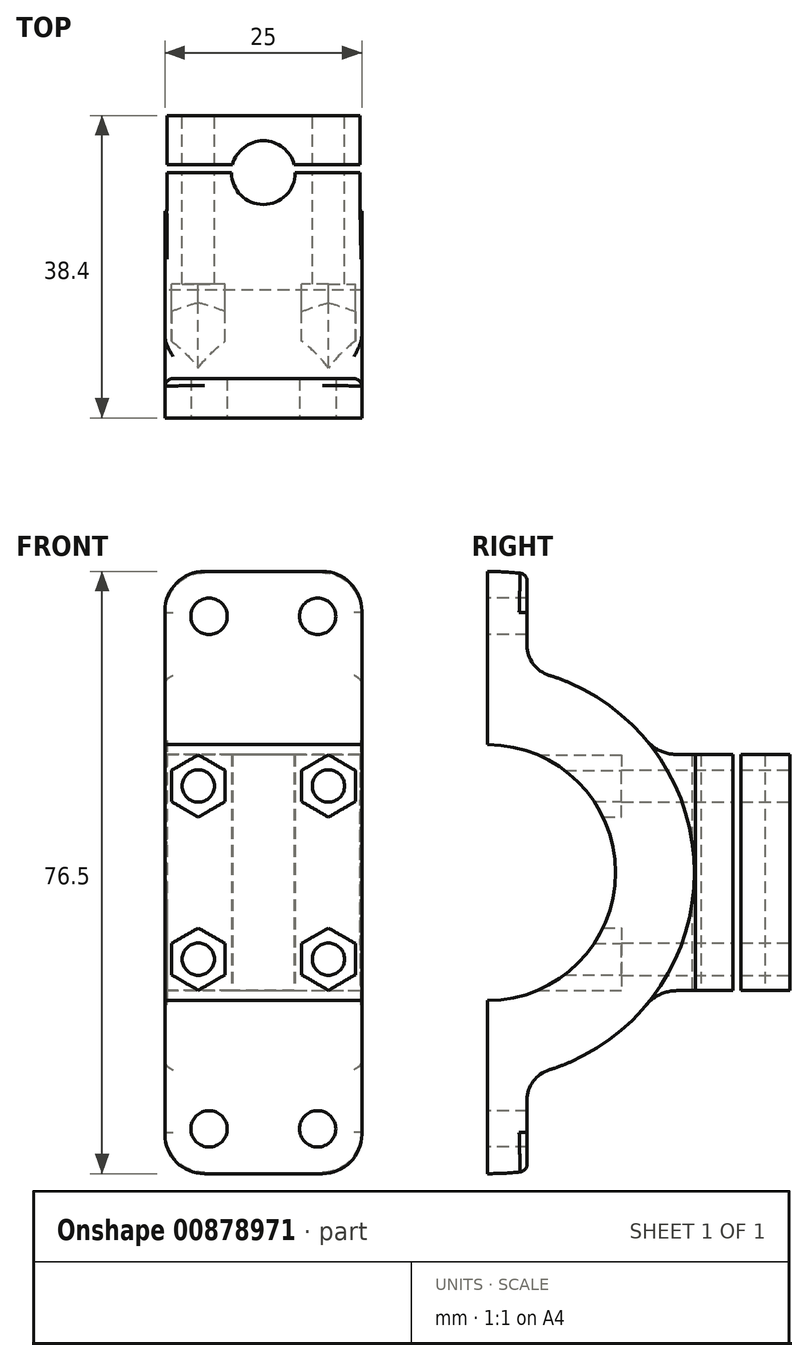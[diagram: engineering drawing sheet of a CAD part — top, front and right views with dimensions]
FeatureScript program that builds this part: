
annotation { "Feature Type Name" : "Feature", "Feature Type Description" : "" }
export const myFeature = defineFeature(function(context is Context, id is Id, definition is map)
    precondition{}
    {
        {
            var Q0;
            Q0=qCreatedBy(makeId("Right.planeOp"),FACE);
            var sketch = newSketch(context, id + "F0", { "sketchPlane" : qUnion([Q0])});
            skArc(sketch, "E0", {"start": v(0, -16.25) * mm, "mid": v(16.25, 0) * mm, "end": v(0, 16.25) * mm});
            skArc(sketch, "E1.0", {"start": v(7.8, -25.06) * mm, "mid": v(26.25, 0) * mm, "end": v(7.8, 25.06) * mm});
            skLineSegment(sketch, "E2", {"start": v(0, 16.25) * mm, "end": v(0, 38.25) * mm});
            skLineSegment(sketch, "E3", {"start": v(0, -16.25) * mm, "end": v(0, -38.25) * mm});
            skLineSegment(sketch, "E4.0", {"start": v(5, -28.88) * mm, "end": v(5, -37.92) * mm});
            skLineSegment(sketch, "E5.0", {"start": v(5, 28.88) * mm, "end": v(5, 37.92) * mm});
            skPoint(sketch, "E6.visualSharp", {"position": v(-5, 25.77) * mm});
            skPoint(sketch, "E7.visualSharp", {"position": v(5, 25.77) * mm});
            skArc(sketch, "E7.filletArc", {"start": v(5, 28.88) * mm, "mid": v(5.78, 26.5) * mm, "end": v(7.8, 25.06) * mm});
            skPoint(sketch, "E8.visualSharp", {"position": v(5, -25.77) * mm});
            skArc(sketch, "E8.filletArc", {"start": v(7.8, -25.06) * mm, "mid": v(5.78, -26.5) * mm, "end": v(5, -28.88) * mm});
            skPoint(sketch, "E9.visualSharp", {"position": v(-5, -25.77) * mm});
            skArc(sketch, "E10.0", {"start": v(5, 37.92) * mm, "mid": v(2.5, 38.17) * mm, "end": v(0, 38.25) * mm});
            skArc(sketch, "E11.MirrorCS", {"start": v(5, -37.92) * mm, "mid": v(2.5, -38.17) * mm, "end": v(0, -38.25) * mm});
            skSolve(sketch);
        }
        {
            var Q0;
            Q0 = qSketchRegion(id + "F0", true);
            extrude(context, id + "F1", {"entities" : qUnion([Q0]), "endBound" : BoundingType.SYMMETRIC, "depth" : 25 * mm, "offsetDistance" : 25 * mm});
        }
        {
            var Q0;
            Q0=qCreatedBy(makeId("Front.planeOp"),FACE);
            var sketch = newSketch(context, id + "F2", { "sketchPlane" : qUnion([Q0])});
            skCircle(sketch, "E12", {"center": v(6.9, 32.56) * mm, "radius": 2.31 * mm});
            skCircle(sketch, "E13.MirrorC", {"center": v(-6.9, 32.56) * mm, "radius": 2.31 * mm});
            skCircle(sketch, "E14.MirrorC", {"center": v(-6.9, -32.56) * mm, "radius": 2.31 * mm});
            skCircle(sketch, "E15.MirrorC", {"center": v(6.9, -32.56) * mm, "radius": 2.31 * mm});
            skSolve(sketch);
        }
        {
            var Q0;
            Q0 = qSketchRegion(id + "F2", true);
            extrude(context, id + "F3", {"entities" : qUnion([Q0]), "operationType" : NewBodyOperationType.REMOVE, "endBound" : BoundingType.THROUGH_ALL, "oppositeDirection" : true, "depth" : 25 * mm, "offsetDistance" : 25 * mm});
        }
        {
            var Q0;
            Q0=qCreatedBy(makeId("Top.planeOp"),FACE);
            var sketch = newSketch(context, id + "F4", { "sketchPlane" : qUnion([Q0])});
            skArc(sketch, "E16", {"start": v(-4.05, 31.16) * mm, "mid": v(0, 27.11) * mm, "end": v(4.05, 31.16) * mm});
            skArc(sketch, "E17", {"start": v(-12.27, 26.35) * mm, "mid": v(-12.27, 26.13) * mm, "end": v(-12.27, 25.92) * mm});
            skLineSegment(sketch, "E18", {"start": v(0, 38.4) * mm, "end": v(-12.27, 38.4) * mm});
            skLineSegment(sketch, "E19", {"start": v(-12.27, 26.35) * mm, "end": v(-12.27, 31.16) * mm});
            skLineSegment(sketch, "E20", {"start": v(10.13, 19.2) * mm, "end": v(-10.13, 19.2) * mm});
            skLineSegment(sketch, "E21", {"start": v(-4.05, 31.16) * mm, "end": v(-12.27, 31.16) * mm});
            skLineSegment(sketch, "E22.0", {"start": v(-3.92, 32.16) * mm, "end": v(-12.27, 32.16) * mm});
            skLineSegment(sketch, "E23.trimOffspring", {"start": v(-12.27, 32.16) * mm, "end": v(-12.27, 38.4) * mm});
            skLineSegment(sketch, "E24", {"start": v(12.26, 26.43) * mm, "end": v(12.44, 19.2) * mm});
            skLineSegment(sketch, "E25", {"start": v(-12.27, 26.35) * mm, "end": v(-12.27, 19.2) * mm});
            skLineSegment(sketch, "E26", {"start": v(-10.13, 19.2) * mm, "end": v(-12.27, 19.2) * mm});
            skLineSegment(sketch, "E27", {"start": v(10.13, 19.2) * mm, "end": v(12.44, 19.2) * mm});
            skLineSegment(sketch, "E28.MirrorCS", {"start": v(0, 38.4) * mm, "end": v(12.27, 38.4) * mm});
            skLineSegment(sketch, "E29.MirrorCS", {"start": v(12.27, 32.16) * mm, "end": v(12.27, 38.4) * mm});
            skLineSegment(sketch, "E30.MirrorCS", {"start": v(3.92, 32.16) * mm, "end": v(12.27, 32.16) * mm});
            skLineSegment(sketch, "E31.MirrorCS", {"start": v(4.05, 31.16) * mm, "end": v(12.27, 31.16) * mm});
            skLineSegment(sketch, "E32.MirrorCS", {"start": v(12.27, 26.35) * mm, "end": v(12.27, 31.16) * mm});
            skArc(sketch, "E33.trimOffspring", {"start": v(3.92, 32.16) * mm, "mid": v(0, 35.21) * mm, "end": v(-3.92, 32.16) * mm});
            skSolve(sketch);
        }
        {
            var Q0;
            Q0 = qSketchRegion(id + "F4", true);
            extrude(context, id + "F5", {"entities" : qUnion([Q0]), "operationType" : NewBodyOperationType.ADD, "endBound" : BoundingType.SYMMETRIC, "depth" : 30 * mm, "offsetDistance" : 25 * mm});
        }
        {
            var Q0;
            Q0=makeQuery(id+"F5.opExtrude","SWEPT_FACE",FACE,{"disambiguationData":[OSD([sQuery(id+"F4.wireOp",EDGE,"E18"),sQuery(id+"F4.wireOp",EDGE,"E28.MirrorCS")])]});
            var sketch = newSketch(context, id + "F6", { "sketchPlane" : qUnion([Q0])});
            skCircle(sketch, "E34", {"center": v(-8.27, 11) * mm, "radius": 2.05 * mm});
            skCircle(sketch, "E35.MirrorC", {"center": v(8.27, 11) * mm, "radius": 2.05 * mm});
            skCircle(sketch, "E36.MirrorC", {"center": v(-8.27, -11) * mm, "radius": 2.05 * mm});
            skCircle(sketch, "E37.MirrorC", {"center": v(8.27, -11) * mm, "radius": 2.05 * mm});
            skPoint(sketch, "E38.0.end.orphan", {"position": v(-12.27, -15) * mm});
            skPoint(sketch, "E38.0.start.orphan", {"position": v(-12.27, 15) * mm});
            skSolve(sketch);
        }
        {
            var Q0;
            Q0 = qSketchRegion(id + "F6", true);
            extrude(context, id + "F7", {"entities" : qUnion([Q0]), "operationType" : NewBodyOperationType.REMOVE, "oppositeDirection" : true, "depth" : 35 * mm, "offsetDistance" : 25 * mm});
        }
        {
            var Q0;
            Q0=qCreatedBy(makeId("Front.planeOp"),FACE);
            cPlane(context, id + "F8", {"entities" : qUnion([Q0]), "cplaneType" : CPlaneType.OFFSET, "offset" : 17 * mm, "oppositeDirection" : true, "width" : 150 * mm, "height" : 150 * mm});
        }
        {
            var Q0;
            Q0=qCreatedBy(id+"F8.planeOp",FACE);
            var sketch = newSketch(context, id + "F9", { "sketchPlane" : qUnion([Q0])});
            skCircle(sketch, "E39.0", {"center": v(8.27, 11) * mm, "radius": 2.05 * mm});
            skCircle(sketch, "E39.1", {"center": v(8.27, -11) * mm, "radius": 2.05 * mm});
            skCircle(sketch, "E40.0", {"center": v(-8.27, 11) * mm, "radius": 2.05 * mm});
            skCircle(sketch, "E41.0", {"center": v(-8.27, -11) * mm, "radius": 2.05 * mm});
            skCircle(sketch, "E42.cCircle", {"center": v(8.27, 11) * mm, "radius": 3.43 * mm, "construction": true});
            skLineSegment(sketch, "E42.0", {"start": v(4.84, 9.02) * mm, "end": v(4.84, 12.98) * mm});
            skLineSegment(sketch, "E42.1", {"start": v(4.84, 12.98) * mm, "end": v(8.27, 14.95) * mm});
            skLineSegment(sketch, "E42.2", {"start": v(8.27, 14.95) * mm, "end": v(11.7, 12.98) * mm});
            skLineSegment(sketch, "E42.3", {"start": v(11.7, 12.98) * mm, "end": v(11.7, 9.02) * mm});
            skLineSegment(sketch, "E42.4", {"start": v(11.7, 9.02) * mm, "end": v(8.27, 7.05) * mm});
            skLineSegment(sketch, "E42.5", {"start": v(8.27, 7.05) * mm, "end": v(4.84, 9.02) * mm});
            skPoint(sketch, "E42.0.midPoint", {"position": v(4.84, 11) * mm});
            skCircle(sketch, "E43.MirrorC", {"center": v(-8.27, 11) * mm, "radius": 3.43 * mm, "construction": true});
            skLineSegment(sketch, "E44.MirrorCS", {"start": v(-4.84, 12.98) * mm, "end": v(-8.27, 14.95) * mm});
            skLineSegment(sketch, "E45.MirrorCS", {"start": v(-8.27, 14.95) * mm, "end": v(-11.7, 12.98) * mm});
            skLineSegment(sketch, "E46.MirrorCS", {"start": v(-11.7, 12.98) * mm, "end": v(-11.7, 9.02) * mm});
            skLineSegment(sketch, "E47.MirrorCS", {"start": v(-11.7, 9.02) * mm, "end": v(-8.27, 7.05) * mm});
            skLineSegment(sketch, "E48.MirrorCS", {"start": v(-8.27, 7.05) * mm, "end": v(-4.84, 9.02) * mm});
            skLineSegment(sketch, "E49.MirrorCS", {"start": v(-4.84, 9.02) * mm, "end": v(-4.84, 12.98) * mm});
            skLineSegment(sketch, "E50.MirrorCS", {"start": v(4.84, -9.02) * mm, "end": v(4.84, -12.98) * mm});
            skLineSegment(sketch, "E51.MirrorCS", {"start": v(-11.7, -12.98) * mm, "end": v(-11.7, -9.02) * mm});
            skLineSegment(sketch, "E52.MirrorCS", {"start": v(8.27, -14.95) * mm, "end": v(11.7, -12.98) * mm});
            skLineSegment(sketch, "E53.MirrorCS", {"start": v(11.7, -9.02) * mm, "end": v(8.27, -7.05) * mm});
            skLineSegment(sketch, "E54.MirrorCS", {"start": v(4.84, -12.98) * mm, "end": v(8.27, -14.95) * mm});
            skLineSegment(sketch, "E55.MirrorCS", {"start": v(-11.7, -9.02) * mm, "end": v(-8.27, -7.05) * mm});
            skPoint(sketch, "E56.MirrorP", {"position": v(4.84, -11) * mm});
            skLineSegment(sketch, "E57.MirrorCS", {"start": v(-8.27, -7.05) * mm, "end": v(-4.84, -9.02) * mm});
            skLineSegment(sketch, "E58.MirrorCS", {"start": v(-4.84, -12.98) * mm, "end": v(-8.27, -14.95) * mm});
            skLineSegment(sketch, "E59.MirrorCS", {"start": v(-8.27, -14.95) * mm, "end": v(-11.7, -12.98) * mm});
            skCircle(sketch, "E60.MirrorC", {"center": v(8.27, -11) * mm, "radius": 3.43 * mm, "construction": true});
            skLineSegment(sketch, "E61.MirrorCS", {"start": v(8.27, -7.05) * mm, "end": v(4.84, -9.02) * mm});
            skLineSegment(sketch, "E62.MirrorCS", {"start": v(-4.84, -9.02) * mm, "end": v(-4.84, -12.98) * mm});
            skLineSegment(sketch, "E63.MirrorCS", {"start": v(11.7, -12.98) * mm, "end": v(11.7, -9.02) * mm});
            skCircle(sketch, "E64.MirrorC", {"center": v(-8.27, -11) * mm, "radius": 3.43 * mm, "construction": true});
            skSolve(sketch);
        }
        {
            var Q0;
            Q0 = qSketchRegion(id + "F9", true);
            extrude(context, id + "F10", {"entities" : qUnion([Q0]), "operationType" : NewBodyOperationType.REMOVE, "depth" : 25 * mm, "offsetDistance" : 25 * mm});
        }
        {
            var Q0;
            Q0=makeQuery(id+"F5.boolean.opBoolean","INTERSECT",EDGE,{"derivedFrom":[makeQuery(id+"F1.opExtrude","SWEPT_FACE",FACE,{"disambiguationData":[OSD([sQuery(id+"F0.wireOp",EDGE,"E1.0")])]}),makeQuery(id+"F5.opExtrude","CAP_FACE",FACE,{"disambiguationData":[OSD([sQuery(id+"F4.wireOp",EDGE,"E16"),sQuery(id+"F4.wireOp",EDGE,"E17"),sQuery(id+"F4.wireOp",EDGE,"E19"),sQuery(id+"F4.wireOp",EDGE,"E20"),sQuery(id+"F4.wireOp",EDGE,"E21"),sQuery(id+"F4.wireOp",EDGE,"E24"),sQuery(id+"F4.wireOp",EDGE,"E25"),sQuery(id+"F4.wireOp",EDGE,"E26"),sQuery(id+"F4.wireOp",EDGE,"E27"),sQuery(id+"F4.wireOp",EDGE,"E31.MirrorCS"),sQuery(id+"F4.wireOp",EDGE,"E32.MirrorCS")])],"isStart":true})]});
            var Q1;
            Q1=makeQuery(id+"F5.boolean.opBoolean","INTERSECT",EDGE,{"derivedFrom":[makeQuery(id+"F1.opExtrude","SWEPT_FACE",FACE,{"disambiguationData":[OSD([sQuery(id+"F0.wireOp",EDGE,"E1.0")])]}),makeQuery(id+"F5.opExtrude","CAP_FACE",FACE,{"disambiguationData":[OSD([sQuery(id+"F4.wireOp",EDGE,"E16"),sQuery(id+"F4.wireOp",EDGE,"E17"),sQuery(id+"F4.wireOp",EDGE,"E19"),sQuery(id+"F4.wireOp",EDGE,"E20"),sQuery(id+"F4.wireOp",EDGE,"E21"),sQuery(id+"F4.wireOp",EDGE,"E24"),sQuery(id+"F4.wireOp",EDGE,"E25"),sQuery(id+"F4.wireOp",EDGE,"E26"),sQuery(id+"F4.wireOp",EDGE,"E27"),sQuery(id+"F4.wireOp",EDGE,"E31.MirrorCS"),sQuery(id+"F4.wireOp",EDGE,"E32.MirrorCS")])],"isStart":false})]});
            fillet(context, id + "F11", {"entities" : qUnion([Q0, Q1]), "radius" : 5 * mm, "tangentPropagation" : true, "allowEdgeOverflow" : false});
        }
        {
            var Q0;
            Q0=makeQuery(id+"F1.opExtrude","CAP_EDGE",EDGE,{"disambiguationData":[OSD([sQuery(id+"F0.wireOp",EDGE,"E10.0")])],"isStart":false});
            var Q1;
            Q1=makeQuery(id+"F1.opExtrude","CAP_EDGE",EDGE,{"disambiguationData":[OSD([sQuery(id+"F0.wireOp",EDGE,"E10.0")])],"isStart":true});
            var Q2;
            Q2=makeQuery(id+"F1.opExtrude","CAP_EDGE",EDGE,{"disambiguationData":[OSD([sQuery(id+"F0.wireOp",EDGE,"E11.MirrorCS")])],"isStart":true});
            var Q3;
            Q3=makeQuery(id+"F1.opExtrude","CAP_EDGE",EDGE,{"disambiguationData":[OSD([sQuery(id+"F0.wireOp",EDGE,"E11.MirrorCS")])],"isStart":false});
            fillet(context, id + "F12", {"entities" : qUnion([Q0, Q1, Q2, Q3]), "radius" : 5 * mm, "tangentPropagation" : true, "allowEdgeOverflow" : false});
        }
        {
            var Q0;
            Q0=makeQuery(id+"F1.opExtrude","CAP_EDGE",EDGE,{"disambiguationData":[OSD([sQuery(id+"F0.wireOp",EDGE,"E4.0")])],"isStart":false});
            var Q1;
            Q1=makeQuery(id+"F12.opFillet","BLEND_EDGE",EDGE,{"blendedFrom":[makeQuery(id+"F1.opExtrude","CAP_EDGE",EDGE,{"disambiguationData":[OSD([sQuery(id+"F0.wireOp",EDGE,"E11.MirrorCS")])],"isStart":false}),makeQuery(id+"F1.opExtrude","SWEPT_FACE",FACE,{"disambiguationData":[OSD([sQuery(id+"F0.wireOp",EDGE,"E4.0")])]})],"blendedInto":[makeQuery(id+"F1.opExtrude","SWEPT_FACE",FACE,{"disambiguationData":[OSD([sQuery(id+"F0.wireOp",EDGE,"E4.0")])]})]});
            var Q2;
            Q2=makeQuery(id+"F1.opExtrude","SWEPT_EDGE",EDGE,{"disambiguationData":[OSD([sQuery(id+"F0.wireOp",EDGE,"E4.0"),sQuery(id+"F0.wireOp",EDGE,"E11.MirrorCS")])]});
            var Q3;
            Q3=makeQuery(id+"F12.opFillet","BLEND_EDGE",EDGE,{"blendedFrom":[makeQuery(id+"F1.opExtrude","CAP_EDGE",EDGE,{"disambiguationData":[OSD([sQuery(id+"F0.wireOp",EDGE,"E11.MirrorCS")])],"isStart":true}),makeQuery(id+"F1.opExtrude","SWEPT_FACE",FACE,{"disambiguationData":[OSD([sQuery(id+"F0.wireOp",EDGE,"E4.0")])]})],"blendedInto":[makeQuery(id+"F1.opExtrude","SWEPT_FACE",FACE,{"disambiguationData":[OSD([sQuery(id+"F0.wireOp",EDGE,"E4.0")])]})]});
            var Q4;
            Q4=makeQuery(id+"F1.opExtrude","CAP_EDGE",EDGE,{"disambiguationData":[OSD([sQuery(id+"F0.wireOp",EDGE,"E4.0")])],"isStart":true});
            var Q5;
            Q5=makeQuery(id+"F1.opExtrude","CAP_EDGE",EDGE,{"disambiguationData":[OSD([sQuery(id+"F0.wireOp",EDGE,"E8.filletArc")])],"isStart":true});
            var Q6;
            Q6=makeQuery(id+"F1.opExtrude","CAP_EDGE",EDGE,{"disambiguationData":[OSD([sQuery(id+"F0.wireOp",EDGE,"E8.filletArc")])],"isStart":false});
            var Q7;
            Q7=makeQuery(id+"F1.opExtrude","CAP_EDGE",EDGE,{"disambiguationData":[OSD([sQuery(id+"F0.wireOp",EDGE,"E7.filletArc")])],"isStart":false});
            var Q8;
            Q8=makeQuery(id+"F1.opExtrude","CAP_EDGE",EDGE,{"disambiguationData":[OSD([sQuery(id+"F0.wireOp",EDGE,"E5.0")])],"isStart":false});
            var Q9;
            Q9=makeQuery(id+"F12.opFillet","BLEND_EDGE",EDGE,{"blendedFrom":[makeQuery(id+"F1.opExtrude","CAP_EDGE",EDGE,{"disambiguationData":[OSD([sQuery(id+"F0.wireOp",EDGE,"E10.0")])],"isStart":false}),makeQuery(id+"F1.opExtrude","SWEPT_FACE",FACE,{"disambiguationData":[OSD([sQuery(id+"F0.wireOp",EDGE,"E5.0")])]})],"blendedInto":[makeQuery(id+"F1.opExtrude","SWEPT_FACE",FACE,{"disambiguationData":[OSD([sQuery(id+"F0.wireOp",EDGE,"E5.0")])]})]});
            var Q10;
            Q10=makeQuery(id+"F1.opExtrude","SWEPT_EDGE",EDGE,{"disambiguationData":[OSD([sQuery(id+"F0.wireOp",EDGE,"E5.0"),sQuery(id+"F0.wireOp",EDGE,"E10.0")])]});
            var Q11;
            Q11=makeQuery(id+"F12.opFillet","BLEND_EDGE",EDGE,{"blendedFrom":[makeQuery(id+"F1.opExtrude","CAP_EDGE",EDGE,{"disambiguationData":[OSD([sQuery(id+"F0.wireOp",EDGE,"E10.0")])],"isStart":true}),makeQuery(id+"F1.opExtrude","SWEPT_FACE",FACE,{"disambiguationData":[OSD([sQuery(id+"F0.wireOp",EDGE,"E5.0")])]})],"blendedInto":[makeQuery(id+"F1.opExtrude","SWEPT_FACE",FACE,{"disambiguationData":[OSD([sQuery(id+"F0.wireOp",EDGE,"E5.0")])]})]});
            var Q12;
            Q12=makeQuery(id+"F1.opExtrude","CAP_EDGE",EDGE,{"disambiguationData":[OSD([sQuery(id+"F0.wireOp",EDGE,"E5.0")])],"isStart":true});
            var Q13;
            Q13=makeQuery(id+"F1.opExtrude","CAP_EDGE",EDGE,{"disambiguationData":[OSD([sQuery(id+"F0.wireOp",EDGE,"E7.filletArc")])],"isStart":true});
            fillet(context, id + "F13", {"entities" : qUnion([Q0, Q1, Q2, Q3, Q4, Q5, Q6, Q7, Q8, Q9, Q10, Q11, Q12, Q13]), "radius" : 1 * mm, "allowEdgeOverflow" : false});
        }
    });
